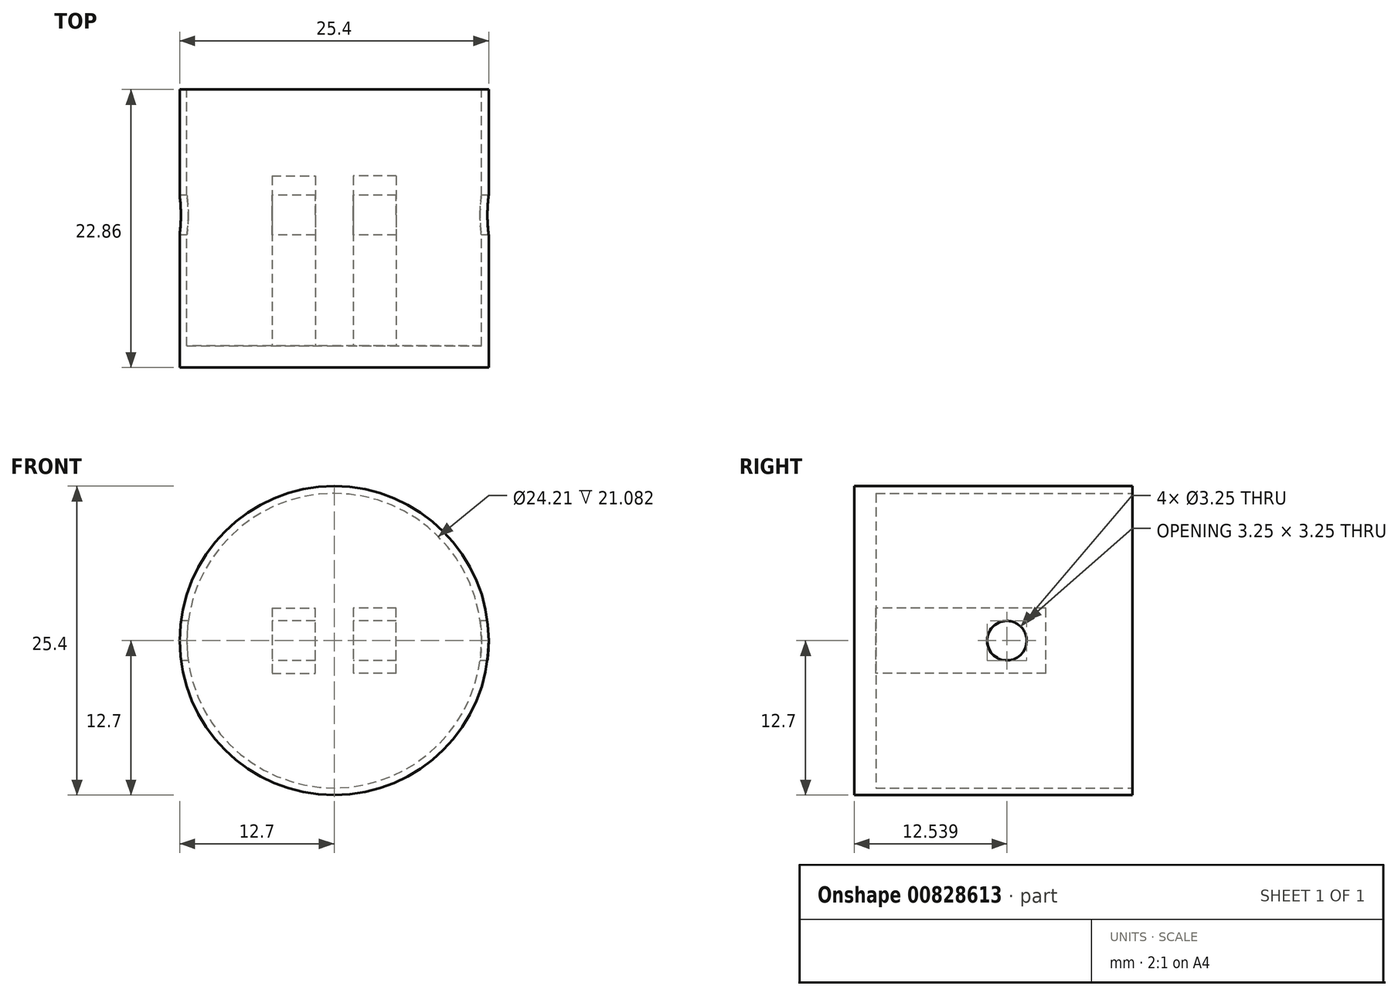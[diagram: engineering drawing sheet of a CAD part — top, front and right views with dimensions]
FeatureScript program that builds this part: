
annotation { "Feature Type Name" : "Feature", "Feature Type Description" : "" }
export const myFeature = defineFeature(function(context is Context, id is Id, definition is map)
    precondition{}
    {
        {
            var Q0;
            Q0=qCreatedBy(makeId("Front.planeOp"),FACE);
            var sketch = newSketch(context, id + "F0", { "sketchPlane" : qUnion([Q0])});
            skCircle(sketch, "E0", {"center": v(0, 0) * mm, "radius": 12.7 * mm});
            skSolve(sketch);
        }
        {
            var Q0;
            Q0 = qSketchRegion(id + "F0", true);
            extrude(context, id + "F1", {"entities" : qUnion([Q0]), "depth" : 22.86 * mm, "offsetDistance" : 25.4 * mm});
        }
        {
            var Q0;
            Q0=makeQuery(id+"F1.opExtrude","CAP_FACE",FACE,{"disambiguationData":[OSD([sQuery(id+"F0.wireOp",EDGE,"E0")])],"isStart":true});
            var sketch = newSketch(context, id + "F2", { "sketchPlane" : qUnion([Q0])});
            skCircle(sketch, "E1", {"center": v(0, 0) * mm, "radius": 12.1 * mm});
            skSolve(sketch);
        }
        {
            var Q0;
            Q0 = qSketchRegion(id + "F2", true);
            extrude(context, id + "F3", {"entities" : qUnion([Q0]), "operationType" : NewBodyOperationType.REMOVE, "oppositeDirection" : true, "depth" : 21.08 * mm, "offsetDistance" : 25.4 * mm});
        }
        {
            var Q0;
            Q0=makeQuery(id+"F3.boolean.opBoolean","COPY",FACE,{"derivedFrom":makeQuery(id+"F3.opExtrude","CAP_FACE",FACE,{"disambiguationData":[OSD([sQuery(id+"F2.wireOp",EDGE,"E1")])],"isStart":false})});
            var sketch = newSketch(context, id + "F4", { "sketchPlane" : qUnion([Q0])});
            skLineSegment(sketch, "E2.top", {"start": v(-5.1, 2.68) * mm, "end": v(-1.55, 2.68) * mm});
            skLineSegment(sketch, "E2.left", {"start": v(-5.1, 0) * mm, "end": v(-5.1, 2.68) * mm});
            skLineSegment(sketch, "E2.right", {"start": v(-1.55, 0) * mm, "end": v(-1.55, 2.68) * mm});
            skLineSegment(sketch, "E3.MirrorCS", {"start": v(-5.1, 0) * mm, "end": v(-5.1, -2.68) * mm});
            skLineSegment(sketch, "E4.MirrorCS", {"start": v(-5.1, -2.68) * mm, "end": v(-1.55, -2.68) * mm});
            skLineSegment(sketch, "E5.MirrorCS", {"start": v(-1.55, 0) * mm, "end": v(-1.55, -2.68) * mm});
            skLineSegment(sketch, "E6.MirrorCS", {"start": v(1.55, 0) * mm, "end": v(1.55, 2.68) * mm});
            skLineSegment(sketch, "E7.MirrorCS", {"start": v(5.1, 2.68) * mm, "end": v(1.55, 2.68) * mm});
            skLineSegment(sketch, "E8.MirrorCS", {"start": v(5.1, 0) * mm, "end": v(5.1, 2.68) * mm});
            skLineSegment(sketch, "E9.MirrorCS", {"start": v(5.1, 0) * mm, "end": v(5.1, -2.68) * mm});
            skLineSegment(sketch, "E10.MirrorCS", {"start": v(5.1, -2.68) * mm, "end": v(1.55, -2.68) * mm});
            skLineSegment(sketch, "E11.MirrorCS", {"start": v(1.55, 0) * mm, "end": v(1.55, -2.68) * mm});
            skSolve(sketch);
        }
        {
            var Q0;
            Q0=makeQuery(id+"F4.imprint","IMPRINT",FACE,{"disambiguationData":[TD([[makeQuery(id+"F4.imprint","IMPRINT",EDGE,{"derivedFrom":sQuery(id+"F4.wireOp",EDGE,"E2.top")}),-1.0]])]});
            var Q1;
            Q1=makeQuery(id+"F4.imprint","IMPRINT",FACE,{"disambiguationData":[TD([[makeQuery(id+"F4.imprint","IMPRINT",EDGE,{"derivedFrom":sQuery(id+"F4.wireOp",EDGE,"E6.MirrorCS")}),-1.0]])]});
            extrude(context, id + "F5", {"entities" : qUnion([Q0, Q1]), "operationType" : NewBodyOperationType.ADD, "depth" : 13.97 * mm, "offsetDistance" : 25.4 * mm});
        }
        {
            var Q0;
            Q0=qCreatedBy(makeId("Right.planeOp"),FACE);
            var sketch = newSketch(context, id + "F6", { "sketchPlane" : qUnion([Q0])});
            skCircle(sketch, "E12", {"center": v(-10.32, 0) * mm, "radius": 1.63 * mm});
            skSolve(sketch);
        }
        {
            var Q0;
            Q0 = qSketchRegion(id + "F6", true);
            extrude(context, id + "F7", {"entities" : qUnion([Q0]), "operationType" : NewBodyOperationType.REMOVE, "endBound" : BoundingType.SYMMETRIC, "depth" : 25.4 * mm, "offsetDistance" : 25.4 * mm});
        }
    });
